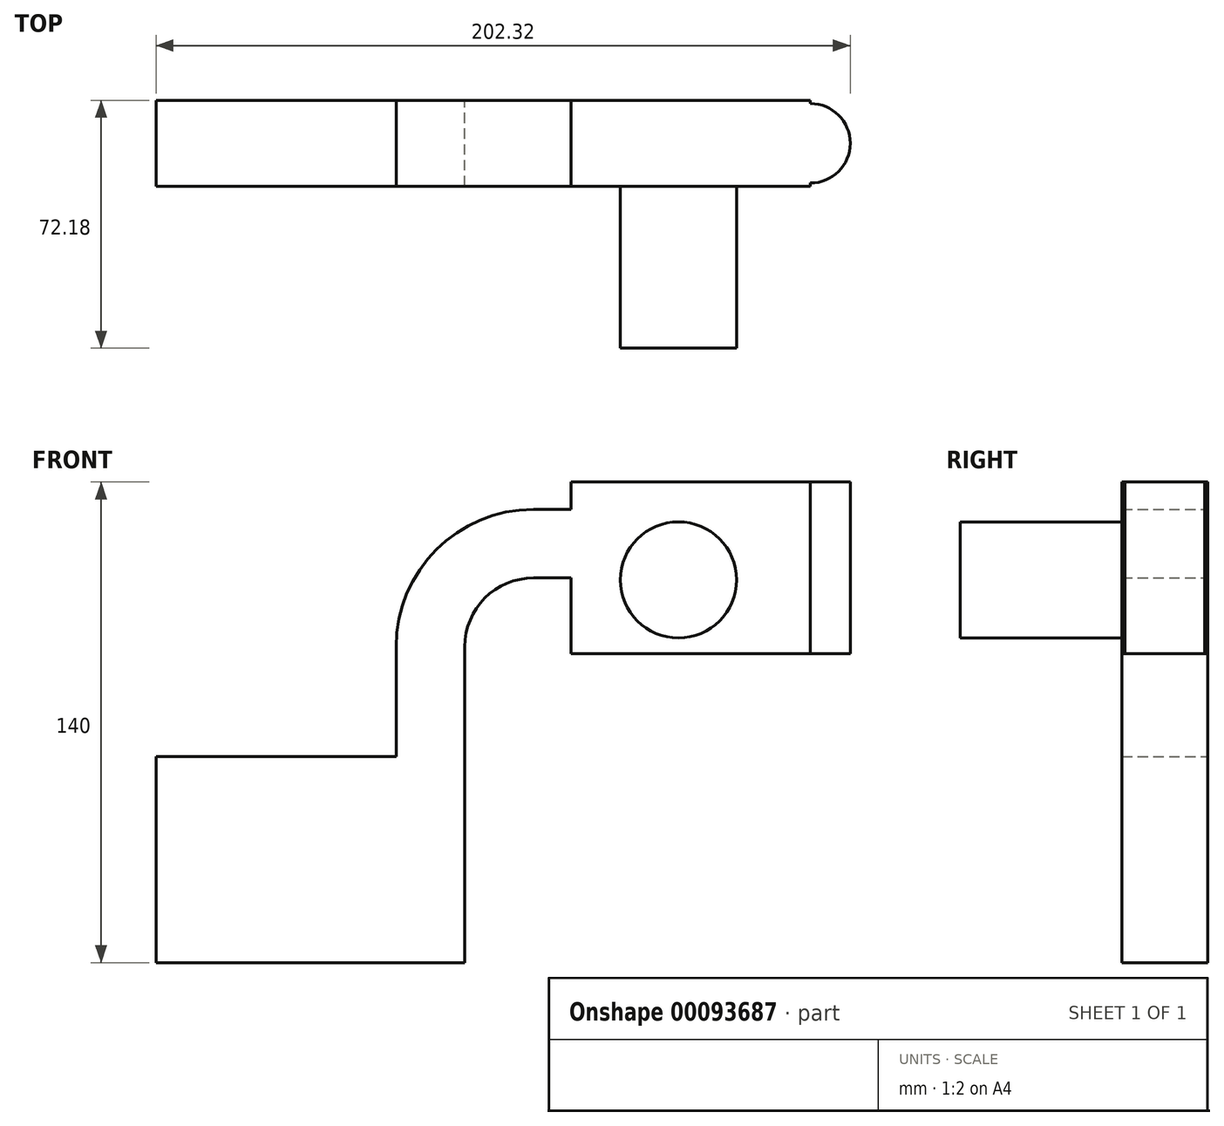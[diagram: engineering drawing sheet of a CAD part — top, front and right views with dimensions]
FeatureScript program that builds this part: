
annotation { "Feature Type Name" : "Feature", "Feature Type Description" : "" }
export const myFeature = defineFeature(function(context is Context, id is Id, definition is map)
    precondition{}
    {
        {
            var Q0;
            Q0=qCreatedBy(makeId("Front.planeOp"),FACE);
            var sketch = newSketch(context, id + "F0", { "sketchPlane" : qUnion([Q0])});
            skLineSegment(sketch, "E0.bottom", {"start": v(-45, 30) * mm, "end": v(45, 30) * mm});
            skLineSegment(sketch, "E0.top", {"start": v(-45, -30) * mm, "end": v(45, -30) * mm});
            skLineSegment(sketch, "E0.left", {"start": v(-45, 30) * mm, "end": v(-45, -30) * mm});
            skLineSegment(sketch, "E0.right", {"start": v(45, 30) * mm, "end": v(45, -30) * mm});
            skPoint(sketch, "E0.middle", {"position": v(0, 0) * mm});
            skLineSegment(sketch, "E1.bottom", {"start": v(145.74, 60) * mm, "end": v(76.02, 60) * mm});
            skLineSegment(sketch, "E1.top", {"start": v(145.74, 110) * mm, "end": v(76.02, 110) * mm});
            skLineSegment(sketch, "E1.left", {"start": v(145.74, 60) * mm, "end": v(145.74, 110) * mm});
            skLineSegment(sketch, "E1.right", {"start": v(76.02, 60) * mm, "end": v(76.02, 110) * mm});
            skPoint(sketch, "E1.middle", {"position": v(110.88, 85) * mm});
            skLineSegment(sketch, "E2", {"start": v(45, 30) * mm, "end": v(45, 62.04) * mm});
            skArc(sketch, "E3", {"start": v(45, 62.04) * mm, "mid": v(50.86, 76.19) * mm, "end": v(65, 82.04) * mm});
            skLineSegment(sketch, "E4", {"start": v(65, 82.04) * mm, "end": v(118.78, 82.04) * mm});
            skLineSegment(sketch, "E5.0", {"start": v(65, 102.04) * mm, "end": v(118.78, 102.04) * mm});
            skArc(sketch, "E5.1", {"start": v(25, 62.04) * mm, "mid": v(36.72, 90.33) * mm, "end": v(65, 102.04) * mm});
            skLineSegment(sketch, "E5.2", {"start": v(25, 30) * mm, "end": v(25, 62.04) * mm});
            skLineSegment(sketch, "E6", {"start": v(118.78, 60) * mm, "end": v(118.78, 110) * mm});
            skFitSpline(sketch, "E7", {"points": [v(-45, 30) * mm, v(65, 102.04) * mm], "startDerivative": vector(-14.03, 205.6) * mm, "endDerivative": vector(137.5, -73) * mm});
            skSolve(sketch);
        }
        {
            var Q0;
            Q0=makeQuery(id+"F0.imprint","IMPRINT",FACE,{"disambiguationData":[TD([[makeQuery(id+"F0.imprint","IMPRINT",EDGE,{"derivedFrom":sQuery(id+"F0.wireOp",EDGE,"E0.top")}),1.0]])]});
            var Q1;
            Q1=makeQuery(id+"F0.imprint","IMPRINT",FACE,{"disambiguationData":[TD([[makeQuery(id+"F0.imprint","IMPRINT",EDGE,{"derivedFrom":sQuery(id+"F0.wireOp",EDGE,"E5.1")}),1.0]])]});
            var Q2;
            {var subQ0=sQuery(id+"F0.wireOp",EDGE,"E1.right");var subQ1=sQuery(id+"F0.wireOp",EDGE,"E1.bottom");var subQ2=makeQuery(id+"F0.imprint","INTERSECT",VERTEX,{"derivedFrom":[subQ1,subQ0]});Q2=makeQuery(id+"F0.imprint","IMPRINT",FACE,{"disambiguationData":[TD([[makeQuery(id+"F0.imprint","IMPRINT",EDGE,{"disambiguationData":[TD([[subQ2,1.0]])],"derivedFrom":subQ1}),-1.0]])]});}
            var Q3;
            {var subQ0=sQuery(id+"F0.wireOp",EDGE,"E1.right");var subQ1=sQuery(id+"F0.wireOp",EDGE,"E1.top");var subQ2=makeQuery(id+"F0.imprint","INTERSECT",VERTEX,{"derivedFrom":[subQ1,subQ0]});Q3=makeQuery(id+"F0.imprint","IMPRINT",FACE,{"disambiguationData":[TD([[makeQuery(id+"F0.imprint","IMPRINT",EDGE,{"disambiguationData":[TD([[subQ2,1.0]])],"derivedFrom":subQ1}),1.0]])]});}
            var Q4;
            {var subQ1=sQuery(id+"F0.wireOp",EDGE,"E2");Q4=makeQuery(id+"F0.imprint","IMPRINT",FACE,{"disambiguationData":[TD([[makeQuery(id+"F0.imprint","IMPRINT",EDGE,{"derivedFrom":subQ1}),1.0]])]});}
            var Q5;
            {var subQ0=sQuery(id+"F0.wireOp",EDGE,"E1.left");Q5=makeQuery(id+"F0.imprint","IMPRINT",FACE,{"disambiguationData":[TD([[makeQuery(id+"F0.imprint","IMPRINT",EDGE,{"derivedFrom":subQ0}),1.0]])]});}
            var Q6;
            {var subQ0=sQuery(id+"F0.wireOp",EDGE,"E4");var subQ1=sQuery(id+"F0.wireOp",EDGE,"E1.right");var subQ2=makeQuery(id+"F0.imprint","INTERSECT",VERTEX,{"derivedFrom":[subQ1,subQ0]});Q6=makeQuery(id+"F0.imprint","IMPRINT",FACE,{"disambiguationData":[TD([[makeQuery(id+"F0.imprint","IMPRINT",EDGE,{"disambiguationData":[TD([[subQ2,-1.0]])],"derivedFrom":subQ1}),-1.0]])]});}
            extrude(context, id + "F1", {"entities" : qUnion([Q0, Q1, Q2, Q3, Q4, Q5, Q6]), "endBound" : BoundingType.SYMMETRIC, "depth" : 25 * mm});
        }
        {
            var Q0;
            Q0=makeQuery(id+"F1.opExtrude","SWEPT_FACE",FACE,{"disambiguationData":[OSD([sQuery(id+"F0.wireOp",EDGE,"E1.top")])]});
            var sketch = newSketch(context, id + "F2", { "sketchPlane" : qUnion([Q0])});
            skCircle(sketch, "E8", {"center": v(145.74, 0) * mm, "radius": 11.58 * mm});
            skSolve(sketch);
        }
        {
            var Q0;
            Q0 = qSketchRegion(id + "F2", true);
            extrude(context, id + "F3", {"entities" : qUnion([Q0]), "operationType" : NewBodyOperationType.ADD, "oppositeDirection" : true, "depth" : 50 * mm});
        }
        {
            var Q0;
            Q0=makeQuery(id+"F1.opExtrude","CAP_FACE",FACE,{"disambiguationData":[OSD([sQuery(id+"F0.wireOp",EDGE,"E0.top"),sQuery(id+"F0.wireOp",EDGE,"E0.left"),sQuery(id+"F0.wireOp",EDGE,"E0.right"),sQuery(id+"F0.wireOp",EDGE,"E1.bottom"),sQuery(id+"F0.wireOp",EDGE,"E1.top"),sQuery(id+"F0.wireOp",EDGE,"E1.left"),sQuery(id+"F0.wireOp",EDGE,"E1.right"),sQuery(id+"F0.wireOp",EDGE,"E2"),sQuery(id+"F0.wireOp",EDGE,"E3"),sQuery(id+"F0.wireOp",EDGE,"E4"),sQuery(id+"F0.wireOp",EDGE,"E5.0"),sQuery(id+"F0.wireOp",EDGE,"E7")])],"isStart":false});
            var sketch = newSketch(context, id + "F4", { "sketchPlane" : qUnion([Q0])});
            skCircle(sketch, "E9", {"center": v(107.28, 81.47) * mm, "radius": 16.93 * mm});
            skSolve(sketch);
        }
        {
            var Q0;
            Q0=makeQuery(id+"F4.imprint","IMPRINT",FACE,{"disambiguationData":[TD([[makeQuery(id+"F4.imprint","IMPRINT",EDGE,{"derivedFrom":sQuery(id+"F4.wireOp",EDGE,"E9")}),1.0]])]});
            extrude(context, id + "F5", {"entities" : qUnion([Q0]), "operationType" : NewBodyOperationType.ADD, "depth" : 47.18 * mm});
        }
    });
